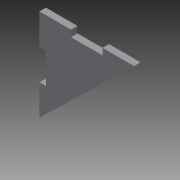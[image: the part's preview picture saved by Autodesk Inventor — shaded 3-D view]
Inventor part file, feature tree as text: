
AUTODESK INVENTOR PART (.ipt)
format: ipt  version: 2013 (Build 170138000, 138)  size: 90,624 bytes
history: native  units: in
note: dims shown in document units (in); Inventor stores cm internally (conversion verified against a paired STEP export)
features: extrude x3, sketch x3
ambient origin geometry x8: Origin, YZ Plane, XZ Plane, XY Plane, X Axis, Y Axis, Z Axis, Center Point
bodies: Solid1 (feature_tree)
feature tree (6):
  extrude  "Extrusion1"  Depth=1.75in
  extrude  "Extrusion2"  TaperAngle=0.0deg  [1 undecoded]
  extrude  "Extrusion3"  Depth=0.124in
  sketch  "Sketch1"  dims[d0=1.8in d1=1.75in]
  sketch  "Sketch2"  dims[d2=0.124in d3=0.0in]
  sketch  "Sketch3"  dims[d4=0.6in d5=0.124in d6=0.6in d7=0.124in d8=0.5833in d9=0.5833in d10=0.124in d11=0.0in d12=0.124in d13=0.0in]
note: 1 required parameter value undecoded (feature->parameter linkage not recoverable at this tier; creation-order binding heuristic only, values carry confidence <= 0.55)
